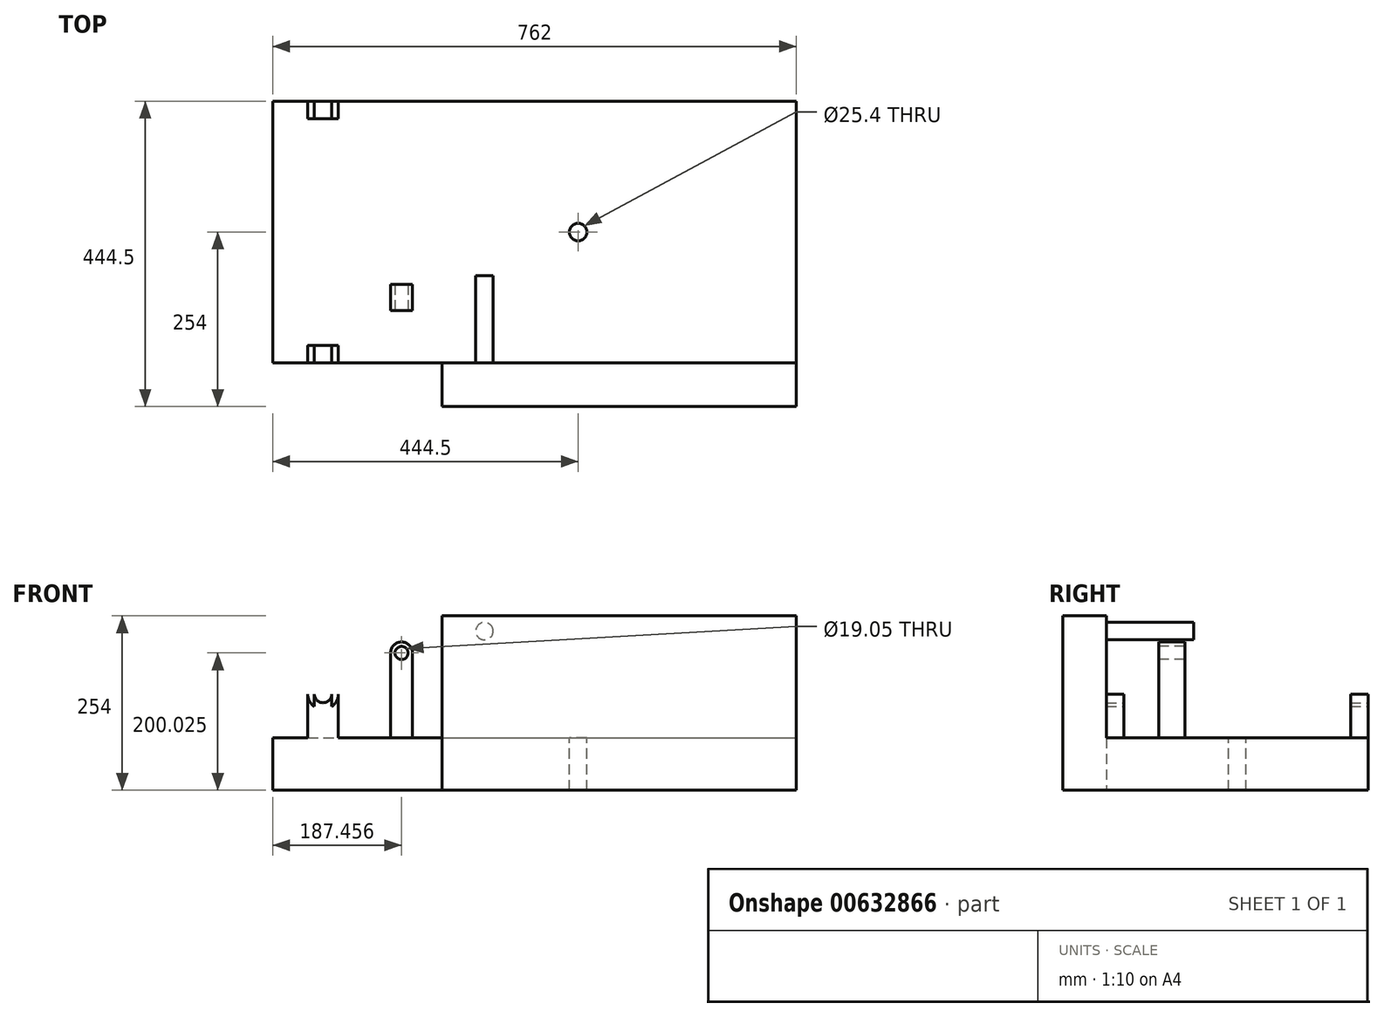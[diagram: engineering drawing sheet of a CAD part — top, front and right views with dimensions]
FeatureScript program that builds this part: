
annotation { "Feature Type Name" : "Feature", "Feature Type Description" : "" }
export const myFeature = defineFeature(function(context is Context, id is Id, definition is map)
    precondition{}
    {
        {
            var Q0;
            Q0=qCreatedBy(makeId("Front.planeOp"),FACE);
            var sketch = newSketch(context, id + "F0", { "sketchPlane" : qUnion([Q0])});
            skLineSegment(sketch, "E0.bottom", {"start": v(-381, 0) * mm, "end": v(381, 0) * mm});
            skLineSegment(sketch, "E0.top", {"start": v(-381, -76.2) * mm, "end": v(381, -76.2) * mm});
            skLineSegment(sketch, "E0.left", {"start": v(-381, 0) * mm, "end": v(-381, -76.2) * mm});
            skLineSegment(sketch, "E0.right", {"start": v(381, 0) * mm, "end": v(381, -76.2) * mm});
            skPoint(sketch, "E1", {"position": v(0, 0) * mm});
            skCircle(sketch, "E2", {"center": v(-307.84, 64.02) * mm, "radius": 12.7 * mm});
            skLineSegment(sketch, "E3", {"start": v(-320.54, 64.02) * mm, "end": v(-320.54, -76.2) * mm});
            skLineSegment(sketch, "E4", {"start": v(-295.14, 64.02) * mm, "end": v(-295.14, -76.2) * mm});
            skCircle(sketch, "E5", {"center": v(-307.84, 64.02) * mm, "radius": 22.23 * mm});
            skLineSegment(sketch, "E6", {"start": v(-330.07, 64.02) * mm, "end": v(-330.07, -76.2) * mm});
            skLineSegment(sketch, "E7", {"start": v(-285.62, 64.02) * mm, "end": v(-285.62, -76.2) * mm});
            skSolve(sketch);
        }
        {
            var Q0;
            Q0=makeQuery(id+"F0.imprint","IMPRINT",FACE,{"disambiguationData":[TD([[makeQuery(id+"F0.imprint","IMPRINT",EDGE,{"derivedFrom":sQuery(id+"F0.wireOp",EDGE,"E0.bottom")}),-1.0]])]});
            extrude(context, id + "F1", {"entities" : qUnion([Q0]), "endBound" : BoundingType.SYMMETRIC, "depth" : 381 * mm, "offsetDistance" : 25.4 * mm});
        }
        {
            var Q0;
            {var subQ0=sQuery(id+"F0.wireOp",EDGE,"E3");var subQ1=sQuery(id+"F0.wireOp",EDGE,"E0.bottom");var subQ2=makeQuery(id+"F0.imprint","INTERSECT",VERTEX,{"derivedFrom":[subQ1,subQ0]});Q0=makeQuery(id+"F0.imprint","IMPRINT",FACE,{"disambiguationData":[TD([[makeQuery(id+"F0.imprint","IMPRINT",EDGE,{"disambiguationData":[TD([[subQ2,-1.0]])],"derivedFrom":subQ1}),1.0]])]});}
            var Q1;
            {var subQ0=sQuery(id+"F0.wireOp",EDGE,"E7");var subQ1=sQuery(id+"F0.wireOp",EDGE,"E0.bottom");var subQ2=makeQuery(id+"F0.imprint","INTERSECT",VERTEX,{"derivedFrom":[subQ1,subQ0]});Q1=makeQuery(id+"F0.imprint","IMPRINT",FACE,{"disambiguationData":[TD([[makeQuery(id+"F0.imprint","IMPRINT",EDGE,{"disambiguationData":[TD([[subQ2,1.0]])],"derivedFrom":subQ1}),1.0]])]});}
            var Q2;
            {var subQ1=sQuery(id+"F0.wireOp",EDGE,"E2");var subQ8=makeQuery(id+"F0.imprint","IMPRINT",VERTEX,{"derivedFrom":subQ1});Q2=makeQuery(id+"F0.imprint","IMPRINT",FACE,{"disambiguationData":[TD([[makeQuery(id+"F0.imprint","IMPRINT",EDGE,{"disambiguationData":[TD([[subQ8,1.0]])],"derivedFrom":subQ1}),-1.0]])]});}
            var Q3;
            {var subQ0=sQuery(id+"F0.wireOp",EDGE,"E6");var subQ1=sQuery(id+"F0.wireOp",EDGE,"E0.bottom");var subQ2=makeQuery(id+"F0.imprint","INTERSECT",VERTEX,{"derivedFrom":[subQ1,subQ0]});Q3=makeQuery(id+"F0.imprint","IMPRINT",FACE,{"disambiguationData":[TD([[makeQuery(id+"F0.imprint","IMPRINT",EDGE,{"disambiguationData":[TD([[subQ2,-1.0]])],"derivedFrom":subQ1}),1.0]])]});}
            var Q4;
            {var subQ0=sQuery(id+"F0.wireOp",EDGE,"E3");var subQ1=sQuery(id+"F0.wireOp",EDGE,"E2");var subQ2=makeQuery(id+"F0.imprint","INTERSECT",VERTEX,{"derivedFrom":[subQ1,subQ0]});Q4=makeQuery(id+"F0.imprint","IMPRINT",FACE,{"disambiguationData":[TD([[makeQuery(id+"F0.imprint","IMPRINT",EDGE,{"disambiguationData":[TD([[subQ2,-1.0]])],"derivedFrom":subQ1}),-1.0]])]});}
            extrude(context, id + "F2", {"entities" : qUnion([Q0, Q1, Q2, Q3, Q4]), "operationType" : NewBodyOperationType.ADD, "endBound" : BoundingType.SYMMETRIC, "depth" : 381 * mm, "offsetDistance" : 25.4 * mm});
        }
        {
            var Q0;
            {var subQ0=sQuery(id+"F0.wireOp",EDGE,"E3");var subQ1=sQuery(id+"F0.wireOp",EDGE,"E0.bottom");var subQ2=makeQuery(id+"F0.imprint","INTERSECT",VERTEX,{"derivedFrom":[subQ1,subQ0]});Q0=makeQuery(id+"F0.imprint","IMPRINT",FACE,{"disambiguationData":[TD([[makeQuery(id+"F0.imprint","IMPRINT",EDGE,{"disambiguationData":[TD([[subQ2,-1.0]])],"derivedFrom":subQ1}),1.0]])]});}
            var Q1;
            {var subQ0=sQuery(id+"F0.wireOp",EDGE,"E3");var subQ1=sQuery(id+"F0.wireOp",EDGE,"E2");var subQ2=makeQuery(id+"F0.imprint","INTERSECT",VERTEX,{"derivedFrom":[subQ1,subQ0]});Q1=makeQuery(id+"F0.imprint","IMPRINT",FACE,{"disambiguationData":[TD([[makeQuery(id+"F0.imprint","IMPRINT",EDGE,{"disambiguationData":[TD([[subQ2,-1.0]])],"derivedFrom":subQ1}),-1.0]])]});}
            var Q2;
            {var subQ1=sQuery(id+"F0.wireOp",EDGE,"E2");var subQ8=makeQuery(id+"F0.imprint","IMPRINT",VERTEX,{"derivedFrom":subQ1});Q2=makeQuery(id+"F0.imprint","IMPRINT",FACE,{"disambiguationData":[TD([[makeQuery(id+"F0.imprint","IMPRINT",EDGE,{"disambiguationData":[TD([[subQ8,1.0]])],"derivedFrom":subQ1}),-1.0]])]});}
            var Q3;
            {var subQ0=sQuery(id+"F0.wireOp",EDGE,"E7");var subQ1=sQuery(id+"F0.wireOp",EDGE,"E0.bottom");var subQ2=makeQuery(id+"F0.imprint","INTERSECT",VERTEX,{"derivedFrom":[subQ1,subQ0]});Q3=makeQuery(id+"F0.imprint","IMPRINT",FACE,{"disambiguationData":[TD([[makeQuery(id+"F0.imprint","IMPRINT",EDGE,{"disambiguationData":[TD([[subQ2,1.0]])],"derivedFrom":subQ1}),1.0]])]});}
            var Q4;
            {var subQ0=sQuery(id+"F0.wireOp",EDGE,"E6");var subQ1=sQuery(id+"F0.wireOp",EDGE,"E0.bottom");var subQ2=makeQuery(id+"F0.imprint","INTERSECT",VERTEX,{"derivedFrom":[subQ1,subQ0]});Q4=makeQuery(id+"F0.imprint","IMPRINT",FACE,{"disambiguationData":[TD([[makeQuery(id+"F0.imprint","IMPRINT",EDGE,{"disambiguationData":[TD([[subQ2,-1.0]])],"derivedFrom":subQ1}),1.0]])]});}
            extrude(context, id + "F3", {"entities" : qUnion([Q0, Q1, Q2, Q3, Q4]), "operationType" : NewBodyOperationType.REMOVE, "endBound" : BoundingType.SYMMETRIC, "oppositeDirection" : true, "depth" : 330.2 * mm, "offsetDistance" : 25.4 * mm});
        }
        {
            var Q0;
            Q0=makeQuery(id+"F1.opExtrude","SWEPT_FACE",FACE,{"disambiguationData":[OSD([sQuery(id+"F0.wireOp",EDGE,"E0.right")])]});
            var sketch = newSketch(context, id + "F4", { "sketchPlane" : qUnion([Q0])});
            skLineSegment(sketch, "E8.bottom", {"start": v(-190.5, -76.2) * mm, "end": v(-254, -76.2) * mm});
            skLineSegment(sketch, "E8.top", {"start": v(-190.5, 177.8) * mm, "end": v(-254, 177.8) * mm});
            skLineSegment(sketch, "E8.left", {"start": v(-190.5, -76.2) * mm, "end": v(-190.5, 177.8) * mm});
            skLineSegment(sketch, "E8.right", {"start": v(-254, -76.2) * mm, "end": v(-254, 177.8) * mm});
            skSolve(sketch);
        }
        {
            var Q0;
            {var subQ4=sQuery(id+"F4.wireOp",EDGE,"E8.bottom");Q0=makeQuery(id+"F4.imprint","IMPRINT",FACE,{"disambiguationData":[TD([[makeQuery(id+"F4.imprint","IMPRINT",EDGE,{"derivedFrom":subQ4}),-1.0]])]});}
            extrude(context, id + "F5", {"entities" : qUnion([Q0]), "operationType" : NewBodyOperationType.ADD, "oppositeDirection" : true, "depth" : 515.62 * mm, "offsetDistance" : 25.4 * mm});
        }
        {
            var Q0;
            {var subQ0=sQuery(id+"F0.wireOp",EDGE,"E0.bottom");var subQ1=sQuery(id+"F0.wireOp",EDGE,"E0.right");var subQ7=sQuery(id+"F0.wireOp",EDGE,"E0.left");var subQ12=makeQuery(id+"F1.opExtrude","SWEPT_FACE",FACE,{"disambiguationData":[OSD([subQ0])]});Q0=makeQuery(id+"F3.boolean.opBoolean","MERGE",FACE,{"derivedFrom":[makeQuery(id+"F2.boolean.opBoolean","SPLIT",FACE,{"disambiguationData":[TD([makeQuery(id+"F1.opExtrude","SWEPT_FACE",FACE,{"disambiguationData":[OSD([subQ7])]})])],"derivedFrom":subQ12}),makeQuery(id+"F2.boolean.opBoolean","SPLIT",FACE,{"disambiguationData":[TD([makeQuery(id+"F1.opExtrude","SWEPT_FACE",FACE,{"disambiguationData":[OSD([subQ1])]})])],"derivedFrom":subQ12}),makeQuery(id+"F3.opExtrude","SWEPT_FACE",FACE,{"disambiguationData":[OSD([subQ0])]})]});}
            var sketch = newSketch(context, id + "F6", { "sketchPlane" : qUnion([Q0])});
            skLineSegment(sketch, "E9.bottom", {"start": v(-177.67, -76.2) * mm, "end": v(-209.42, -76.2) * mm});
            skLineSegment(sketch, "E9.top", {"start": v(-177.67, -114.3) * mm, "end": v(-209.42, -114.3) * mm});
            skLineSegment(sketch, "E9.left", {"start": v(-177.67, -76.2) * mm, "end": v(-177.67, -114.3) * mm});
            skLineSegment(sketch, "E9.right", {"start": v(-209.42, -76.2) * mm, "end": v(-209.42, -114.3) * mm});
            skSolve(sketch);
        }
        {
            var Q0;
            Q0=makeQuery(id+"F6.imprint","IMPRINT",FACE,{"disambiguationData":[TD([[makeQuery(id+"F6.imprint","IMPRINT",EDGE,{"derivedFrom":sQuery(id+"F6.wireOp",EDGE,"E9.bottom")}),1.0]])]});
            extrude(context, id + "F7", {"entities" : qUnion([Q0]), "operationType" : NewBodyOperationType.ADD, "depth" : 139.7 * mm, "offsetDistance" : 25.4 * mm});
        }
        {
            var Q0;
            Q0=makeQuery(id+"F7.opExtrude","SWEPT_FACE",FACE,{"disambiguationData":[OSD([sQuery(id+"F6.wireOp",EDGE,"E9.top")])]});
            var sketch = newSketch(context, id + "F8", { "sketchPlane" : qUnion([Q0])});
            skPoint(sketch, "E10", {"position": v(-193.54, 139.7) * mm});
            skLineSegment(sketch, "E11", {"start": v(-209.42, 123.83) * mm, "end": v(-177.67, 123.83) * mm});
            skLineSegment(sketch, "E12", {"start": v(-193.54, 139.7) * mm, "end": v(-193.54, 0) * mm});
            skPoint(sketch, "E13", {"position": v(-193.54, 123.83) * mm});
            skLineSegment(sketch, "E14.bottom", {"start": v(-177.67, 114.3) * mm, "end": v(-209.42, 114.3) * mm});
            skLineSegment(sketch, "E14.top", {"start": v(-177.67, 133.35) * mm, "end": v(-209.42, 133.35) * mm});
            skLineSegment(sketch, "E14.left", {"start": v(-177.67, 114.3) * mm, "end": v(-177.67, 133.35) * mm});
            skLineSegment(sketch, "E14.right", {"start": v(-209.42, 114.3) * mm, "end": v(-209.42, 133.35) * mm});
            skCircle(sketch, "E15", {"center": v(-193.54, 123.83) * mm, "radius": 9.53 * mm});
            skCircle(sketch, "E16", {"center": v(-193.54, 123.83) * mm, "radius": 15.88 * mm});
            skSolve(sketch);
        }
        {
            var Q0;
            Q0=sQuery(id+"F8.wireOp",VERTEX,"E13");
            var Q1;
            Q1=makeQuery(id+"F1.opExtrude","SWEPT_BODY",BODY,{"disambiguationData":[OSD([sQuery(id+"F0.wireOp",EDGE,"E0.bottom"),sQuery(id+"F0.wireOp",EDGE,"E0.top"),sQuery(id+"F0.wireOp",EDGE,"E0.left"),sQuery(id+"F0.wireOp",EDGE,"E0.right")])]});
            hole(context, id + "F9", {"style" : HoleStyle.SIMPLE, "endStyle" : HoleEndStyle.THROUGH, "holeDiameter" : 19.05 * mm, "majorDiameter" : 6.35 * mm, "isTappedThrough" : true, "tappedDepth" : 12.7 * mm, "tapClearance" : 3, "locations" : qUnion([Q0]), "scope" : qUnion([Q1])});
        }
        {
            var Q0;
            {var subQ0=sQuery(id+"F8.wireOp",EDGE,"E14.top");var subQ4=sQuery(id+"F8.wireOp",EDGE,"E16");var subQ5=makeQuery(id+"F8.imprint","INTERSECT",VERTEX,{"disambiguationData":[OD(0.0)],"derivedFrom":[subQ0,subQ4]});Q0=makeQuery(id+"F8.imprint","IMPRINT",FACE,{"disambiguationData":[TD([[makeQuery(id+"F8.imprint","IMPRINT",EDGE,{"disambiguationData":[TD([[subQ5,-1.0]])],"derivedFrom":subQ4}),-1.0]])]});}
            var Q1;
            {var subQ1=sQuery(id+"F8.wireOp",EDGE,"E14.top");var subQ3=sQuery(id+"F8.wireOp",EDGE,"E16");var subQ4=makeQuery(id+"F8.imprint","INTERSECT",VERTEX,{"disambiguationData":[OD(0.0)],"derivedFrom":[subQ1,subQ3]});Q1=makeQuery(id+"F8.imprint","IMPRINT",FACE,{"disambiguationData":[TD([[makeQuery(id+"F8.imprint","IMPRINT",EDGE,{"disambiguationData":[TD([[subQ4,1.0]])],"derivedFrom":subQ3}),-1.0]])]});}
            var Q2;
            {var subQ0=sQuery(id+"F8.wireOp",EDGE,"E14.top");var subQ4=sQuery(id+"F8.wireOp",EDGE,"E16");var subQ5=makeQuery(id+"F8.imprint","INTERSECT",VERTEX,{"disambiguationData":[OD(1.0)],"derivedFrom":[subQ0,subQ4]});Q2=makeQuery(id+"F8.imprint","IMPRINT",FACE,{"disambiguationData":[TD([[makeQuery(id+"F8.imprint","IMPRINT",EDGE,{"disambiguationData":[TD([[subQ5,1.0]])],"derivedFrom":subQ4}),-1.0]])]});}
            var Q3;
            {var subQ1=sQuery(id+"F8.wireOp",EDGE,"E14.top");var subQ3=sQuery(id+"F8.wireOp",EDGE,"E16");var subQ4=makeQuery(id+"F8.imprint","INTERSECT",VERTEX,{"disambiguationData":[OD(1.0)],"derivedFrom":[subQ1,subQ3]});Q3=makeQuery(id+"F8.imprint","IMPRINT",FACE,{"disambiguationData":[TD([[makeQuery(id+"F8.imprint","IMPRINT",EDGE,{"disambiguationData":[TD([[subQ4,-1.0]])],"derivedFrom":subQ3}),-1.0]])]});}
            extrude(context, id + "F10", {"entities" : qUnion([Q0, Q1, Q2, Q3]), "operationType" : NewBodyOperationType.REMOVE, "oppositeDirection" : true, "depth" : 53.36 * mm, "offsetDistance" : 25.4 * mm});
        }
        {
            var Q0;
            Q0=makeQuery(id+"F5.opExtrude","SWEPT_FACE",FACE,{"disambiguationData":[OSD([sQuery(id+"F4.wireOp",EDGE,"E8.right")])]});
            var sketch = newSketch(context, id + "F11", { "sketchPlane" : qUnion([Q0])});
            skCircle(sketch, "E17", {"center": v(-72.9, 155.58) * mm, "radius": 12.7 * mm});
            skSolve(sketch);
        }
        {
            var Q0;
            Q0=makeQuery(id+"F11.imprint","IMPRINT",FACE,{"disambiguationData":[TD([[makeQuery(id+"F11.imprint","IMPRINT",EDGE,{"derivedFrom":sQuery(id+"F11.wireOp",EDGE,"E17")}),1.0]])]});
            extrude(context, id + "F12", {"entities" : qUnion([Q0]), "operationType" : NewBodyOperationType.ADD, "oppositeDirection" : true, "depth" : 190.5 * mm, "offsetDistance" : 25.4 * mm});
        }
        {
            var Q0;
            {var subQ0=sQuery(id+"F0.wireOp",EDGE,"E0.bottom");var subQ1=sQuery(id+"F0.wireOp",EDGE,"E0.right");var subQ7=sQuery(id+"F0.wireOp",EDGE,"E0.left");var subQ12=makeQuery(id+"F1.opExtrude","SWEPT_FACE",FACE,{"disambiguationData":[OSD([subQ0])]});Q0=makeQuery(id+"F3.boolean.opBoolean","MERGE",FACE,{"derivedFrom":[makeQuery(id+"F2.boolean.opBoolean","SPLIT",FACE,{"disambiguationData":[TD([makeQuery(id+"F1.opExtrude","SWEPT_FACE",FACE,{"disambiguationData":[OSD([subQ7])]})])],"derivedFrom":subQ12}),makeQuery(id+"F2.boolean.opBoolean","SPLIT",FACE,{"disambiguationData":[TD([makeQuery(id+"F1.opExtrude","SWEPT_FACE",FACE,{"disambiguationData":[OSD([subQ1])]})])],"derivedFrom":subQ12}),makeQuery(id+"F3.opExtrude","SWEPT_FACE",FACE,{"disambiguationData":[OSD([subQ0])]})]});}
            var sketch = newSketch(context, id + "F13", { "sketchPlane" : qUnion([Q0])});
            skCircle(sketch, "E18", {"center": v(63.5, 0) * mm, "radius": 12.7 * mm});
            skSolve(sketch);
        }
        {
            var Q0;
            Q0=makeQuery(id+"F13.imprint","IMPRINT",FACE,{"disambiguationData":[TD([[makeQuery(id+"F13.imprint","IMPRINT",EDGE,{"derivedFrom":sQuery(id+"F13.wireOp",EDGE,"E18")}),1.0]])]});
            extrude(context, id + "F14", {"entities" : qUnion([Q0]), "operationType" : NewBodyOperationType.REMOVE, "endBound" : BoundingType.THROUGH_ALL, "oppositeDirection" : true, "depth" : 25.4 * mm, "offsetDistance" : 25.4 * mm});
        }
    });
